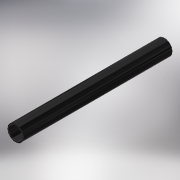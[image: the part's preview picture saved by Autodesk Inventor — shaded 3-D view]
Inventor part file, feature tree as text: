
AUTODESK INVENTOR PART (.ipt)
format: ipt  version: 2018 (Build 220112000, 112)  size: 125,440 bytes
history: native  units: mm
features: extrude x1, other x1
ambient origin geometry x8: Origin, YZ Plane, XZ Plane, XY Plane, X Axis, Y Axis, Z Axis, Center Point
bodies: Solid1 (feature_tree)
feature tree (2):
  extrude  "Tube"  TaperAngle=0.0deg  [1 undecoded]
  other  "Circles"
note: 1 required parameter value undecoded (feature->parameter linkage not recoverable at this tier; creation-order binding heuristic only, values carry confidence <= 0.55)
